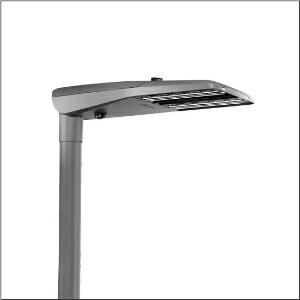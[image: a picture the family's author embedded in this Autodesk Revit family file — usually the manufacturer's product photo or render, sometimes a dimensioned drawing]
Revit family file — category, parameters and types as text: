
# Revit family: streetlight_sl_11_iq_midi___st0_5a_5xc3b51y08me_9d3e
name_source: partatom
category: Lighting Fixtures
units: mm (PartAtom-declared; Revit-internal decimal feet)

## family parameters
Cut with Voids When Loaded = No
Host = Face
Light Source = No
Part Type = Normal
Room Calculation Point = No
Round Connector Dimension = Use Diameter
Shared = No

## types (1)
- --- (1 x LED, 17940 lm, 122.7 W, 3000K)
    Apparent Load = 123 VA
    CIE Flux Codes = 43 74 97 100 100
    Color Rendering = 70
    Color Temperature = 3000K
    Default Elevation = 1800 mm
    Description = Streetlight SL 11 iQ midi, mast luminaire, primary light control with 3 zone facetted reflector, of plastic, silver coated, highly specular, primary optical cover: cover, of PMMA, transparent, light distribution: ST0.5a, light emission: direct distribution, primary light characteristic: asymmetric, installation type: post-top, side-entry, LED, High Power LED, rated luminous flux: 17.940lm, luminous efficacy: 146lm/W, light colour: 730, colour temperature: 3000K, control: presetting dimming logarithmic, Street-Remote, Auto-Match, Temp-Guard, Lumen-Switch, Night-Set, Smart-Wire, Light-Fading, Desk-Remote (wireless, voltage-free reading and setting of iQ features in the workshop via application-optimized NFC function/RFID function), optimised constant luminous flux control (CLO 2.0), with cable H07RN-F 5x 1.5mm², mains connection: 230..240V, AC, 50/60Hz, connection cable pre-assembled, cable length: 12,5m, start of lifetime: 123W, end of service life: 130W, reduction: 56W, luminaire housing, of diecast aluminium, powder-coated, Siteco® metallic grey (DB 702S), please order mast flange separately, inclination adjustable without tools: 0°, 5°, 10°, 15° (post-top) | 0°, -5°, -10°, -15° (side-entry), sealing non-destructively replaceable, multi-level sealing system, length: 780mm, width: 376mm, height: 118mm, mast flange for spigot size: 42mm (side-entry): 5XC10008XM4, 60/48mm (side-entry/post-top): 5XC10108XM2, 76/60mm (side-entry/post-top): 5XC10108XM1, equipment: Power, Smart Interface below and above, protection rating (complete): IP66, insulation class (complete): insulation class II (safety insulation), certification: CE, ENEC, VDE, UKCA, impact resistance: IK09, permissible operating ambient temperature for outdoor applications: -25..+50°C, standard-compliant lighting for roads and squares, Environmental Product Declaration (EPD) tested and certified by an independent institute, packaging unit: 1 piece

Light Distribution: ST0.5a
    Height = 118 mm
    Lamp = 1 x LED
    Lamp Light Flux = 17940 lm
    Lamp Power = 122.7 W
    Lamp count = 1
    Length = 780 mm
    Luminous efficacy = 146 lm/W
    Manufacturer = Siteco
    ModVariant = No
    Model = 5XC3B51Y08ME
    Number of Poles = 1
    OnlyDefault = Yes
    Power Factor = 1
    Product Name = Streetlight SL 11 iQ midi | ST0.5a
    Product group = mast luminaire | pylon top
    ProductGroupID = 6100
    Protection Class = Protection class II
    Protection Degree = IP 66
    RLX_Detail_Level = 1
    RLX_Emergency_Light_Flux = 0 lm
    RLX_Emergency_Type = 0
    RLX_Emergency_Type_DB = No
    RlxData = <blob elided: 74461 chars, md5=6ff75614>
    Socket = socket
    Standby Power = 0 W
    System Light Flux = 17940 lm
    System Power = 123 W
    Type Comments = factory setting: luminous flux: 100 % | dim-lin: 254 | 553 mA
    Type Image = l_1004429.jpg
    URL = http://relux.com
    VarID = @adj_064181
    Voltage = 0 V
    Weight = 0.00 kg
    Width = 376 mm

## geometry (parser evidence)
native form markers: Blend x4, Sweep x12
no freeform markers — native parametric forms only
